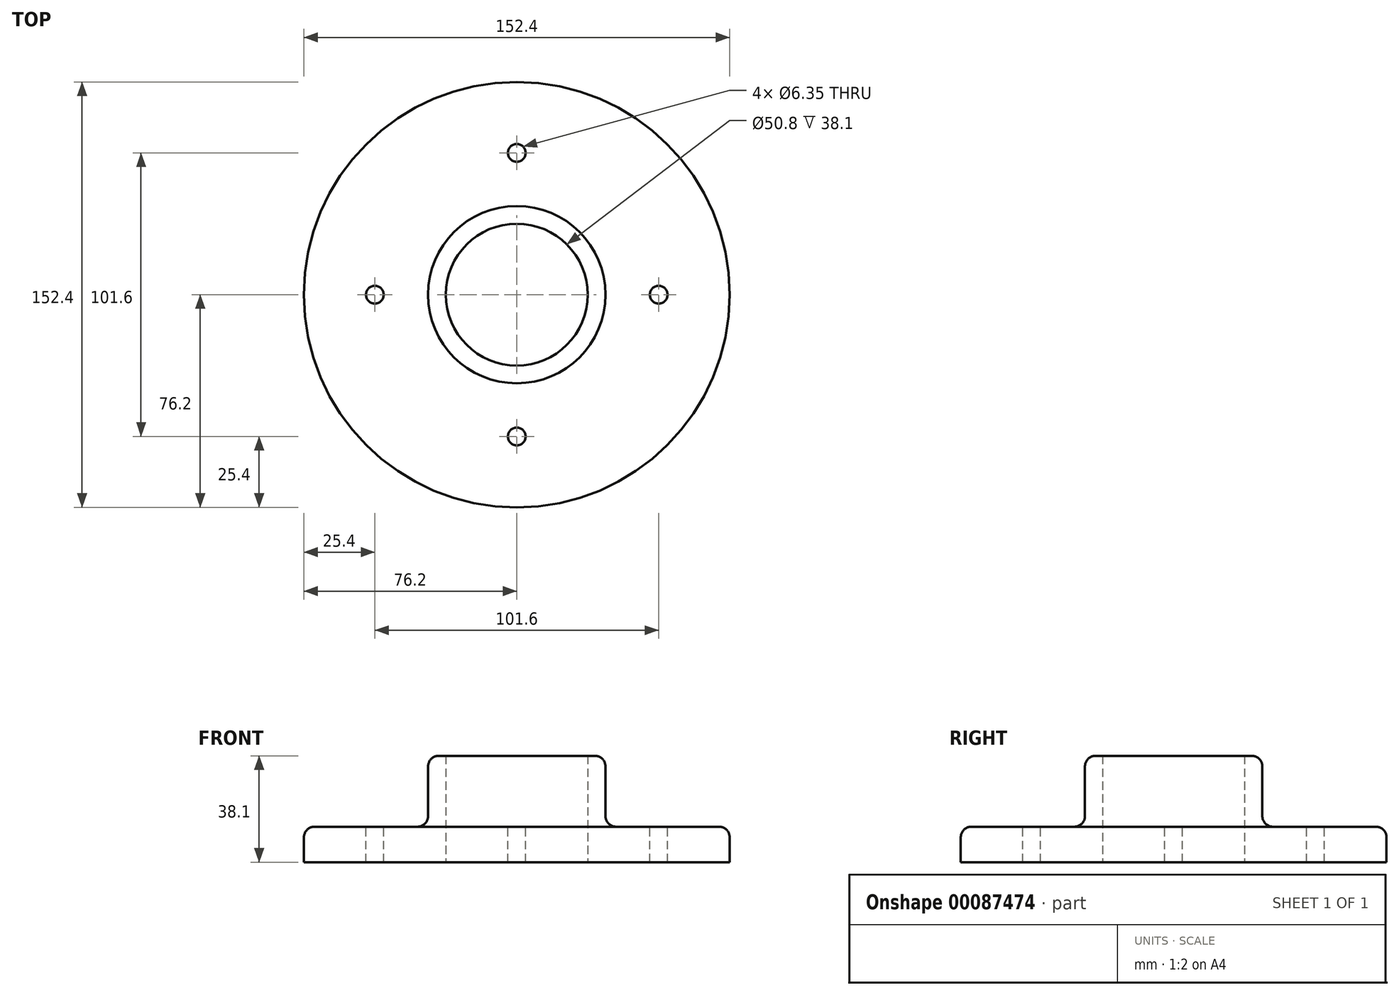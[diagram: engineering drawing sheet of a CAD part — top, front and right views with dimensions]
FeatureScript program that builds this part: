
annotation { "Feature Type Name" : "Feature", "Feature Type Description" : "" }
export const myFeature = defineFeature(function(context is Context, id is Id, definition is map)
    precondition{}
    {
        {
            var Q0;
            Q0=qCreatedBy(makeId("Top.planeOp"),FACE);
            var sketch = newSketch(context, id + "F0", { "sketchPlane" : qUnion([Q0])});
            skCircle(sketch, "E0", {"center": v(0, 0) * mm, "radius": 76.2 * mm});
            skCircle(sketch, "E1", {"center": v(0, 0) * mm, "radius": 25.4 * mm});
            skSolve(sketch);
        }
        {
            var Q0;
            Q0=makeQuery(id+"F0.imprint","IMPRINT",FACE,{"disambiguationData":[TD([[makeQuery(id+"F0.imprint","IMPRINT",EDGE,{"derivedFrom":sQuery(id+"F0.wireOp",EDGE,"E0")}),1.0]])]});
            extrude(context, id + "F1", {"entities" : qUnion([Q0]), "depth" : 12.7 * mm});
        }
        {
            var Q0;
            Q0=qCreatedBy(makeId("Top.planeOp"),FACE);
            var sketch = newSketch(context, id + "F2", { "sketchPlane" : qUnion([Q0])});
            skCircle(sketch, "E2", {"center": v(0, 0) * mm, "radius": 31.75 * mm});
            skCircle(sketch, "E3", {"center": v(0, 0) * mm, "radius": 25.4 * mm});
            skSolve(sketch);
        }
        {
            var Q0;
            Q0=makeQuery(id+"F2.imprint","IMPRINT",FACE,{"disambiguationData":[TD([[makeQuery(id+"F2.imprint","IMPRINT",EDGE,{"derivedFrom":sQuery(id+"F2.wireOp",EDGE,"E2")}),1.0]])]});
            extrude(context, id + "F3", {"entities" : qUnion([Q0]), "operationType" : NewBodyOperationType.ADD, "depth" : 38.1 * mm});
        }
        {
            var Q0;
            Q0=makeQuery(id+"F1.opExtrude","CAP_FACE",FACE,{"disambiguationData":[OSD([sQuery(id+"F0.wireOp",EDGE,"E0"),sQuery(id+"F0.wireOp",EDGE,"E1")])],"isStart":false});
            var sketch = newSketch(context, id + "F4", { "sketchPlane" : qUnion([Q0])});
            skCircle(sketch, "E4", {"center": v(-50.8, 0) * mm, "radius": 3.18 * mm});
            skCircle(sketch, "E5.1.0", {"center": v(0, -50.8) * mm, "radius": 3.18 * mm});
            skCircle(sketch, "E5.2.0", {"center": v(50.8, 0) * mm, "radius": 3.18 * mm});
            skCircle(sketch, "E5.3.0", {"center": v(0, 50.8) * mm, "radius": 3.18 * mm});
            skPoint(sketch, "E5.center", {"position": v(0, 0) * mm});
            skSolve(sketch);
        }
        {
            var Q0;
            Q0 = qSketchRegion(id + "F4", true);
            extrude(context, id + "F5", {"entities" : qUnion([Q0]), "operationType" : NewBodyOperationType.REMOVE, "endBound" : BoundingType.THROUGH_ALL, "oppositeDirection" : true, "depth" : 25.4 * mm});
        }
        {
            var Q0;
            Q0=makeQuery(id+"F1.opExtrude","CAP_EDGE",EDGE,{"disambiguationData":[OSD([sQuery(id+"F0.wireOp",EDGE,"E0")])],"isStart":false});
            var Q1;
            Q1=makeQuery(id+"F3.opExtrude","CAP_EDGE",EDGE,{"disambiguationData":[OSD([sQuery(id+"F2.wireOp",EDGE,"E2")])],"isStart":false});
            var Q2;
            Q2=makeQuery(id+"F3.boolean.opBoolean","INTERSECT",EDGE,{"derivedFrom":[makeQuery(id+"F1.opExtrude","CAP_FACE",FACE,{"disambiguationData":[OSD([sQuery(id+"F0.wireOp",EDGE,"E0"),sQuery(id+"F0.wireOp",EDGE,"E1")])],"isStart":false}),makeQuery(id+"F3.opExtrude","SWEPT_FACE",FACE,{"disambiguationData":[OSD([sQuery(id+"F2.wireOp",EDGE,"E2")])]})]});
            fillet(context, id + "F6", {"entities" : qUnion([Q0, Q1, Q2]), "radius" : 3.8 * mm, "tangentPropagation" : true, "allowEdgeOverflow" : false});
        }
    });
